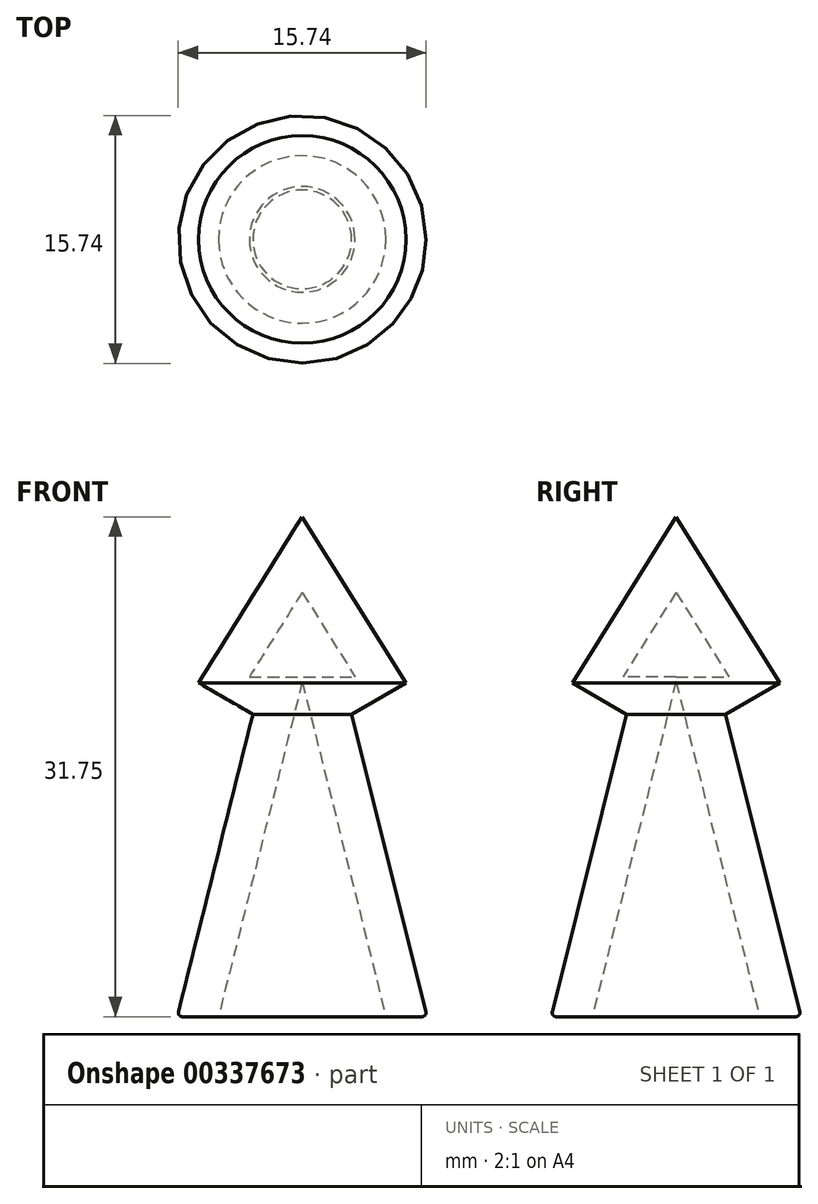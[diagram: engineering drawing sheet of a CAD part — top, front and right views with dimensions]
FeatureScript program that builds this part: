
annotation { "Feature Type Name" : "Feature", "Feature Type Description" : "" }
export const myFeature = defineFeature(function(context is Context, id is Id, definition is map)
    precondition{}
    {
        {
            var Q0;
            Q0=qCreatedBy(makeId("Top.planeOp"),FACE);
            var sketch = newSketch(context, id + "F0", { "sketchPlane" : qUnion([Q0])});
            skCircle(sketch, "E0", {"center": v(0, 0) * mm, "radius": 7.94 * mm});
            skSolve(sketch);
        }
        {
            var Q0;
            Q0=qCreatedBy(makeId("Top.planeOp"),FACE);
            cPlane(context, id + "F1", {"entities" : qUnion([Q0]), "cplaneType" : CPlaneType.OFFSET, "offset" : 12.7 * mm, "width" : 152.4 * mm, "height" : 152.4 * mm});
        }
        {
            var Q0;
            Q0=qCreatedBy(id+"F1.planeOp",FACE);
            var sketch = newSketch(context, id + "F2", { "sketchPlane" : qUnion([Q0])});
            skPoint(sketch, "E1", {"position": v(0, 0) * mm});
            skSolve(sketch);
        }
        {
            var Q0;
            Q0=makeQuery(id+"F0.imprint","IMPRINT",FACE,{"disambiguationData":[TD([[makeQuery(id+"F0.imprint","IMPRINT",EDGE,{"derivedFrom":sQuery(id+"F0.wireOp",EDGE,"E0")}),1.0]])]});
            var Q1;
            Q1=sQuery(id+"F2.wireOp",VERTEX,"E1");
            loft(context, id + "F3", {"sheetProfilesArray" : [{ "sheetProfileEntities" : qUnion([Q0]) }, { "sheetProfileEntities" : qUnion([Q1]) }]});
        }
        {
            var Q0;
            Q0=qCreatedBy(makeId("Top.planeOp"),FACE);
            var sketch = newSketch(context, id + "F4", { "sketchPlane" : qUnion([Q0])});
            skCircle(sketch, "E2", {"center": v(0, 0) * mm, "radius": 3.17 * mm});
            skSolve(sketch);
        }
        {
            var Q0;
            Q0=qCreatedBy(makeId("Top.planeOp"),FACE);
            cPlane(context, id + "F5", {"entities" : qUnion([Q0]), "cplaneType" : CPlaneType.OFFSET, "offset" : 19.05 * mm, "oppositeDirection" : true, "width" : 152.4 * mm, "height" : 152.4 * mm});
        }
        {
            var Q0;
            Q0=qCreatedBy(id+"F5.planeOp",FACE);
            var sketch = newSketch(context, id + "F6", { "sketchPlane" : qUnion([Q0])});
            skCircle(sketch, "E3", {"center": v(0, 0) * mm, "radius": 7.94 * mm});
            skSolve(sketch);
        }
        {
            var Q1;
            Q1=makeQuery(id+"F4.imprint","IMPRINT",FACE,{"disambiguationData":[TD([[makeQuery(id+"F4.imprint","IMPRINT",EDGE,{"derivedFrom":sQuery(id+"F4.wireOp",EDGE,"E2")}),1.0]])]});
            var Q2;
            Q2=makeQuery(id+"F6.imprint","IMPRINT",FACE,{"disambiguationData":[TD([[makeQuery(id+"F6.imprint","IMPRINT",EDGE,{"derivedFrom":sQuery(id+"F6.wireOp",EDGE,"E3")}),1.0]])]});
            loft(context, id + "F7", {"operationType" : NewBodyOperationType.ADD, "sheetProfilesArray" : [{ "sheetProfileEntities" : qUnion([Q1]) }, { "sheetProfileEntities" : qUnion([Q2]) }]});
        }
        {
            var Q0;
            Q0=makeQuery(id+"F7.opLoft","CAP_FACE",FACE,{"disambiguationData":[OSD([makeQuery(id+"F6.imprint","IMPRINT",FACE,{"disambiguationData":[TD([[makeQuery(id+"F6.imprint","IMPRINT",EDGE,{"derivedFrom":sQuery(id+"F6.wireOp",EDGE,"E3")}),1.0]])]})])],"isStart":true});
            shell(context, id + "F8", {"entities" : qUnion([Q0]), "thickness" : 2.54 * mm});
        }
        {
            var Q0;
            Q0=makeQuery(id+"F7.opLoft","MID_CAP_EDGE",EDGE,{"disambiguationData":[OSD([sQuery(id+"F4.wireOp",EDGE,"E2"),sQuery(id+"F6.wireOp",EDGE,"E3")])],"capPos":1.0});
            fillet(context, id + "F9", {"entities" : qUnion([Q0]), "radius" : 0.25 * mm, "tangentPropagation" : true, "allowEdgeOverflow" : false});
        }
        {
            var Q0;
            Q0=makeQuery(id+"F3.opLoft","MID_CAP_EDGE",EDGE,{"disambiguationData":[OSD([sQuery(id+"F0.wireOp",EDGE,"E0"),sQuery(id+"F2.wireOp",VERTEX,"E1")])],"capPos":0.0});
            chamfer(context, id + "F10", {"entities" : qUnion([Q0]), "chamferType" : ChamferType.OFFSET_ANGLE, "width" : 5.08 * mm, "oppositeDirection" : true, "angle" : 30 * degree, "tangentPropagation" : true});
        }
    });
